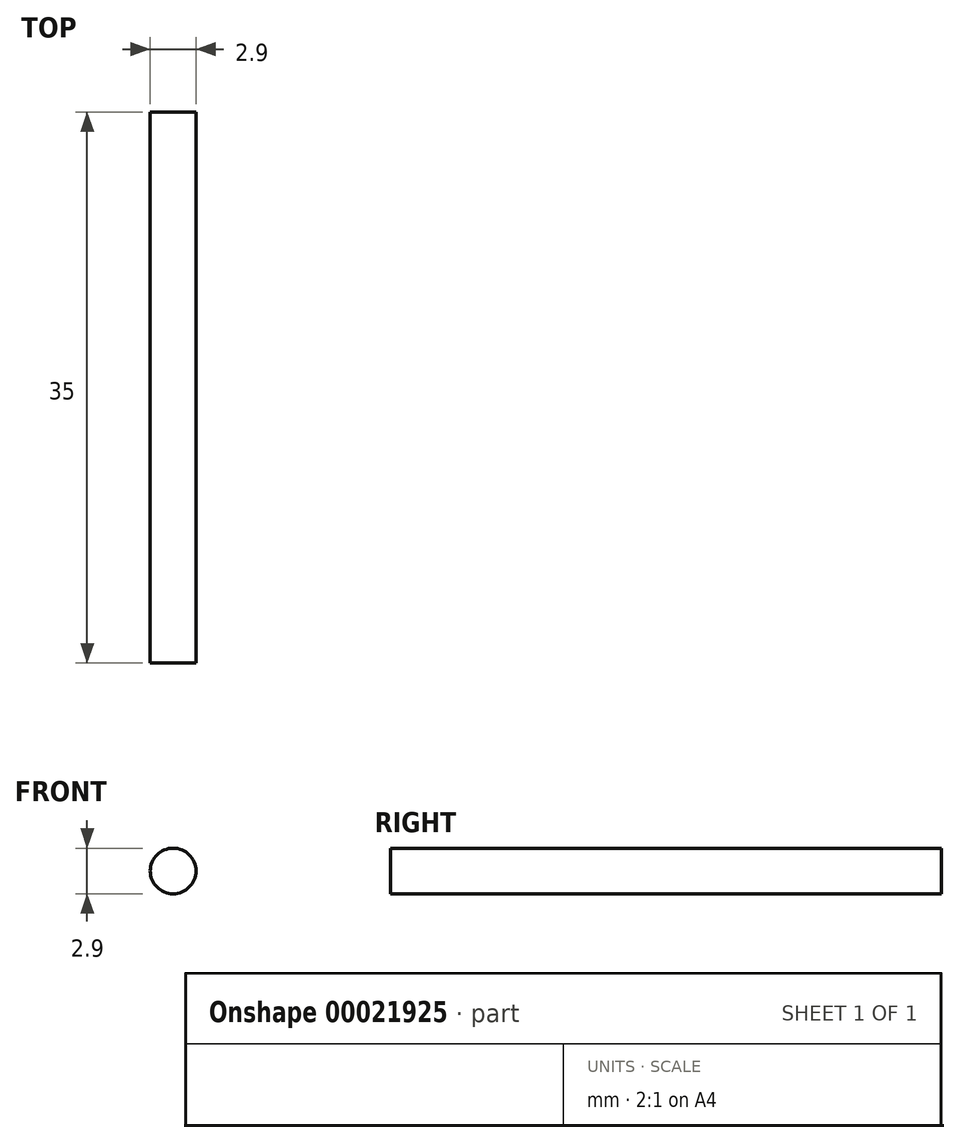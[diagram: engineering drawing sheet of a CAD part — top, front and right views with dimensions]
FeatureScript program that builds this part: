
annotation { "Feature Type Name" : "Feature", "Feature Type Description" : "" }
export const myFeature = defineFeature(function(context is Context, id is Id, definition is map)
    precondition{}
    {
        {
            var Q0;
            Q0=qCreatedBy(makeId("Front.planeOp"),FACE);
            var sketch = newSketch(context, id + "F0", { "sketchPlane" : qUnion([Q0])});
            skCircle(sketch, "E0", {"center": v(0, 0) * mm, "radius": 1.45 * mm});
            skSolve(sketch);
        }
        {
            var Q0;
            Q0=makeQuery(id+"F0.imprint","IMPRINT",FACE,{"disambiguationData":[TD([[makeQuery(id+"F0.imprint","IMPRINT",EDGE,{"derivedFrom":sQuery(id+"F0.wireOp",EDGE,"E0")}),1.0]])]});
            extrude(context, id + "F1", {"entities" : qUnion([Q0]), "depth" : 35 * mm});
        }
    });
